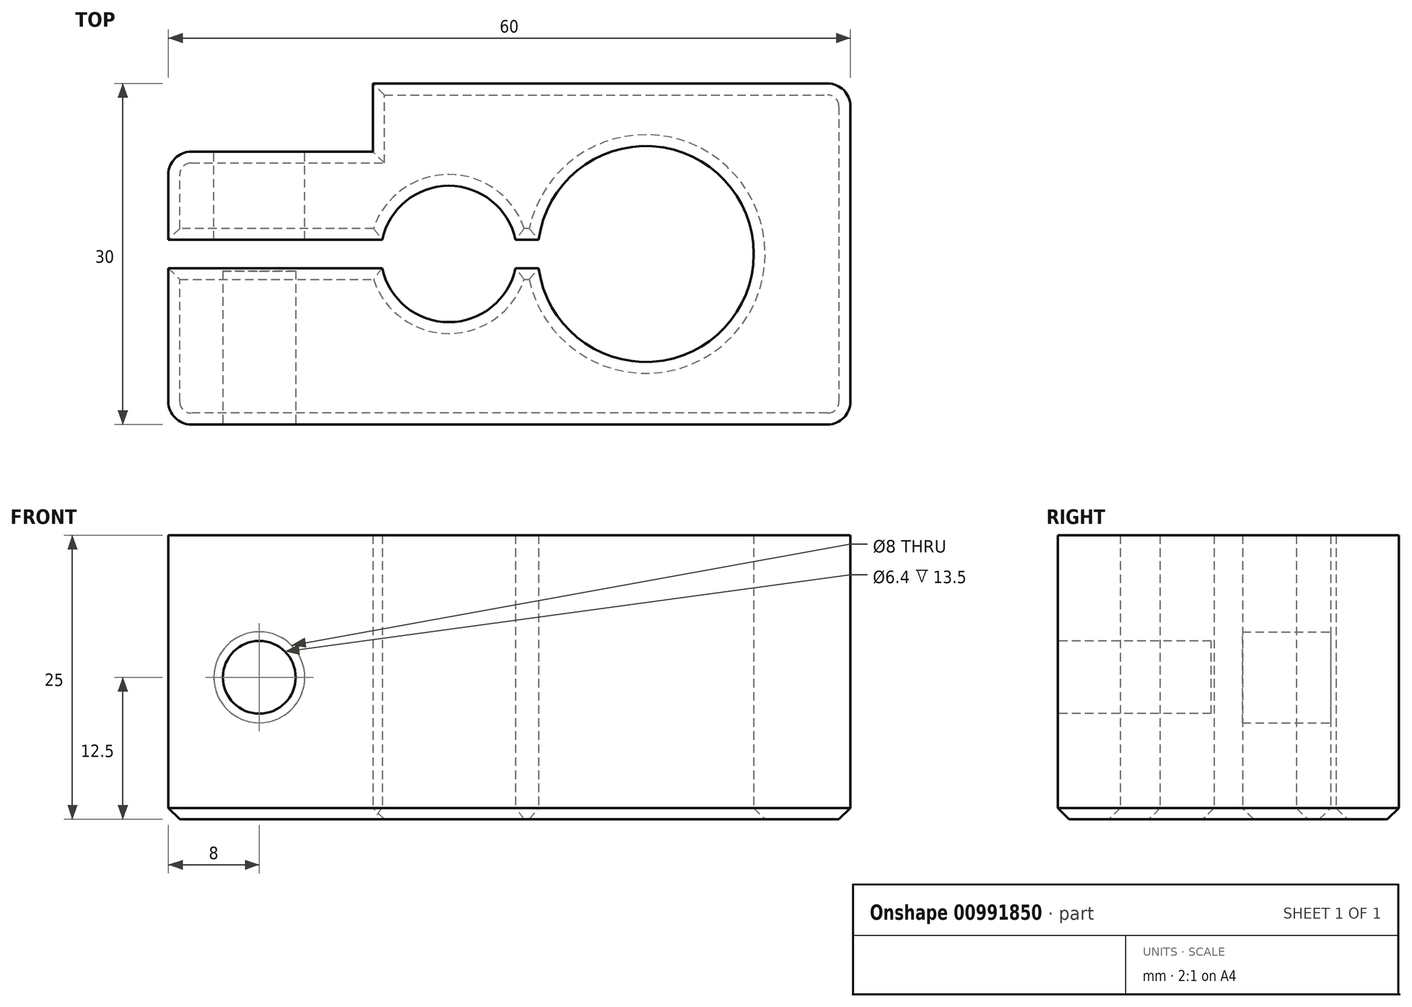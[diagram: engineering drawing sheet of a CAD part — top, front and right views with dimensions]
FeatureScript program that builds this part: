
annotation { "Feature Type Name" : "Feature", "Feature Type Description" : "" }
export const myFeature = defineFeature(function(context is Context, id is Id, definition is map)
    precondition{}
    {
        {
            var Q0;
            Q0=qCreatedBy(makeId("Top.planeOp"),FACE);
            var sketch = newSketch(context, id + "F0", { "sketchPlane" : qUnion([Q0])});
            skLineSegment(sketch, "E0.bottom", {"start": v(-30, -15) * mm, "end": v(30, -15) * mm});
            skLineSegment(sketch, "E0.top", {"start": v(-12, 15) * mm, "end": v(30, 15) * mm});
            skLineSegment(sketch, "E0.left", {"start": v(-30, -15) * mm, "end": v(-30, -1.25) * mm});
            skLineSegment(sketch, "E0.right", {"start": v(30, -15) * mm, "end": v(30, 15) * mm});
            skPoint(sketch, "E0.middle", {"position": v(0, 0) * mm});
            skArc(sketch, "E1", {"start": v(2.58, -1.25) * mm, "mid": v(21.5, 0) * mm, "end": v(2.58, 1.25) * mm});
            skPoint(sketch, "E1.centerSnap0", {"position": v(30, 0) * mm});
            skLineSegment(sketch, "E2.0", {"start": v(2.58, -1.25) * mm, "end": v(0.54, -1.25) * mm});
            skLineSegment(sketch, "E3.MirrorCS", {"start": v(2.58, 1.25) * mm, "end": v(0.54, 1.25) * mm});
            skLineSegment(sketch, "E4.bottom", {"start": v(-30, 9) * mm, "end": v(-12, 9) * mm});
            skLineSegment(sketch, "E4.right", {"start": v(-12, 9) * mm, "end": v(-12, 15) * mm});
            skPoint(sketch, "E5.orphan", {"position": v(-30, 15) * mm});
            skLineSegment(sketch, "E6.trimOffspring", {"start": v(-30, 1.25) * mm, "end": v(-30, 9) * mm});
            skPoint(sketch, "E7.orphan", {"position": v(-30, 0) * mm});
            skPoint(sketch, "E8.orphan", {"position": v(12, 1.25) * mm});
            skPoint(sketch, "E9.orphan", {"position": v(12, -1.25) * mm});
            skArc(sketch, "E10", {"start": v(-11.2, -1.25) * mm, "mid": v(-5.33, -6) * mm, "end": v(0.54, -1.25) * mm});
            skLineSegment(sketch, "E11.trimOffspring", {"start": v(-11.2, 1.25) * mm, "end": v(-30, 1.25) * mm});
            skLineSegment(sketch, "E12.trimOffspring", {"start": v(-11.2, -1.25) * mm, "end": v(-30, -1.25) * mm});
            skArc(sketch, "E13.trimOffspring", {"start": v(0.54, 1.25) * mm, "mid": v(-5.33, 6) * mm, "end": v(-11.2, 1.25) * mm});
            skSolve(sketch);
        }
        {
            var Q0;
            {var subQ0=sQuery(id+"F0.wireOp",EDGE,"vUOmMUN2-ITeZ-OMyY-D1eo-R2V7DhT7ZGRL");var subQ1=sQuery(id+"F0.wireOp",EDGE,"E0.left");var subQ2=makeQuery(id+"F0.imprint","INTERSECT",VERTEX,{"derivedFrom":[subQ1,subQ0]});Q0=makeQuery(id+"F0.imprint","IMPRINT",FACE,{"disambiguationData":[TD([[makeQuery(id+"F0.imprint","IMPRINT",EDGE,{"disambiguationData":[TD([[subQ2,1.0]])],"derivedFrom":subQ1}),-1.0]])]});}
            var Q1;
            {var subQ0=sQuery(id+"F0.wireOp",EDGE,"vUOmMUN2-ITeZ-OMyY-D1eo-R2V7DhT7ZGRL");var subQ1=sQuery(id+"F0.wireOp",EDGE,"E0.left");var subQ2=makeQuery(id+"F0.imprint","INTERSECT",VERTEX,{"derivedFrom":[subQ1,subQ0]});Q1=makeQuery(id+"F0.imprint","IMPRINT",FACE,{"disambiguationData":[TD([[makeQuery(id+"F0.imprint","IMPRINT",EDGE,{"disambiguationData":[TD([[subQ2,-1.0]])],"derivedFrom":subQ1}),-1.0]])]});}
            var Q2;
            {var subQ1=sQuery(id+"F0.wireOp",EDGE,"E0.bottom");Q2=makeQuery(id+"F0.imprint","IMPRINT",FACE,{"disambiguationData":[TD([[makeQuery(id+"F0.imprint","IMPRINT",EDGE,{"derivedFrom":subQ1}),1.0]])]});}
            extrude(context, id + "F1", {"entities" : qUnion([Q0, Q1, Q2]), "depth" : 15 * mm, "offsetDistance" : 25 * mm});
        }
        {
            var Q0;
            Q0 = qSketchRegion(id + "F0", true);
            var Q1;
            Q1=makeQuery(id+"F1.opExtrude","CAP_FACE",FACE,{"disambiguationData":[OSD([sQuery(id+"F0.wireOp",EDGE,"E0.bottom"),sQuery(id+"F0.wireOp",EDGE,"E0.top"),sQuery(id+"F0.wireOp",EDGE,"E0.left"),sQuery(id+"F0.wireOp",EDGE,"E0.right"),sQuery(id+"F0.wireOp",EDGE,"E1"),sQuery(id+"F0.wireOp",EDGE,"E4.bottom"),sQuery(id+"F0.wireOp",EDGE,"E4.right")])],"isStart":true});
            extrude(context, id + "F2", {"entities" : qUnion([Q0, Q1]), "operationType" : NewBodyOperationType.ADD, "depth" : 25 * mm, "offsetDistance" : 25 * mm});
        }
        {
            var Q0;
            Q0 = qSketchRegion(id + "F0", true);
            extrude(context, id + "F3", {"entities" : qUnion([Q0]), "operationType" : NewBodyOperationType.ADD, "depth" : 25 * mm, "offsetDistance" : 25 * mm});
        }
        {
            var Q0;
            {var subQ0=sQuery(id+"F0.wireOp",EDGE,"E4.bottom");Q0=makeQuery(id+"F2.boolean.opBoolean","MERGE",FACE,{"derivedFrom":[makeQuery(id+"F1.opExtrude","SWEPT_FACE",FACE,{"disambiguationData":[OSD([subQ0])]}),makeQuery(id+"F2.opExtrude","SWEPT_FACE",FACE,{"disambiguationData":[OSD([subQ0]),TDD([makeQuery(id+"F0.imprint","IMPRINT",EDGE,{"derivedFrom":subQ0})])]})]});}
            var sketch = newSketch(context, id + "F4", { "sketchPlane" : qUnion([Q0])});
            skCircle(sketch, "E14", {"center": v(22, 12.5) * mm, "radius": 4 * mm});
            skPoint(sketch, "E14.centerSnap0", {"position": v(30, 12.5) * mm});
            skSolve(sketch);
        }
        {
            var Q0;
            Q0=makeQuery(id+"F4.imprint","IMPRINT",FACE,{"disambiguationData":[TD([[makeQuery(id+"F4.imprint","IMPRINT",EDGE,{"derivedFrom":sQuery(id+"F4.wireOp",EDGE,"E14")}),1.0]])]});
            extrude(context, id + "F5", {"entities" : qUnion([Q0]), "operationType" : NewBodyOperationType.REMOVE, "oppositeDirection" : true, "depth" : 9 * mm, "offsetDistance" : 25 * mm});
        }
        {
            var Q0;
            {var subQ0=sQuery(id+"F0.wireOp",EDGE,"E0.bottom");Q0=makeQuery(id+"F2.boolean.opBoolean","MERGE",FACE,{"derivedFrom":[makeQuery(id+"F1.opExtrude","SWEPT_FACE",FACE,{"disambiguationData":[OSD([subQ0])]}),makeQuery(id+"F2.opExtrude","SWEPT_FACE",FACE,{"disambiguationData":[OSD([subQ0]),TDD([makeQuery(id+"F0.imprint","IMPRINT",EDGE,{"derivedFrom":subQ0})])]})]});}
            var sketch = newSketch(context, id + "F6", { "sketchPlane" : qUnion([Q0])});
            skCircle(sketch, "E15", {"center": v(-22, 12.5) * mm, "radius": 3.2 * mm});
            skPoint(sketch, "E15.centerSnap0", {"position": v(-30, 12.5) * mm});
            skSolve(sketch);
        }
        {
            var Q0;
            Q0 = qSketchRegion(id + "F6", true);
            extrude(context, id + "F7", {"entities" : qUnion([Q0]), "operationType" : NewBodyOperationType.REMOVE, "oppositeDirection" : true, "depth" : 13.5 * mm, "offsetDistance" : 25 * mm});
        }
        {
            var Q0;
            {var subQ0=sQuery(id+"F0.wireOp",EDGE,"E0.right");var subQ1=sQuery(id+"F0.wireOp",EDGE,"E0.bottom");Q0=makeQuery(id+"F2.boolean.opBoolean","MERGE",EDGE,{"derivedFrom":[makeQuery(id+"F1.opExtrude","SWEPT_EDGE",EDGE,{"disambiguationData":[OSD([subQ1,subQ0])]}),makeQuery(id+"F2.opExtrude","SWEPT_EDGE",EDGE,{"disambiguationData":[OSD([subQ1,subQ0]),TDD([makeQuery(id+"F0.imprint","INTERSECT",VERTEX,{"derivedFrom":[subQ1,subQ0]})])]})]});}
            var Q1;
            {var subQ0=sQuery(id+"F0.wireOp",EDGE,"E0.right");var subQ1=sQuery(id+"F0.wireOp",EDGE,"E0.top");Q1=makeQuery(id+"F2.boolean.opBoolean","MERGE",EDGE,{"derivedFrom":[makeQuery(id+"F1.opExtrude","SWEPT_EDGE",EDGE,{"disambiguationData":[OSD([subQ1,subQ0])]}),makeQuery(id+"F2.opExtrude","SWEPT_EDGE",EDGE,{"disambiguationData":[OSD([subQ1,subQ0]),TDD([makeQuery(id+"F0.imprint","INTERSECT",VERTEX,{"derivedFrom":[subQ1,subQ0]})])]})]});}
            var Q2;
            {var subQ0=sQuery(id+"F0.wireOp",EDGE,"E0.left");var subQ1=sQuery(id+"F0.wireOp",EDGE,"E0.bottom");Q2=makeQuery(id+"F2.boolean.opBoolean","MERGE",EDGE,{"derivedFrom":[makeQuery(id+"F1.opExtrude","SWEPT_EDGE",EDGE,{"disambiguationData":[OSD([subQ1,subQ0])]}),makeQuery(id+"F2.opExtrude","SWEPT_EDGE",EDGE,{"disambiguationData":[OSD([subQ1,subQ0]),TDD([makeQuery(id+"F0.imprint","INTERSECT",VERTEX,{"derivedFrom":[subQ1,subQ0]})])]})]});}
            var Q3;
            {var subQ0=sQuery(id+"F0.wireOp",EDGE,"E6.trimOffspring");var subQ1=sQuery(id+"F0.wireOp",EDGE,"E4.bottom");Q3=makeQuery(id+"F2.boolean.opBoolean","MERGE",EDGE,{"derivedFrom":[makeQuery(id+"F1.opExtrude","SWEPT_EDGE",EDGE,{"disambiguationData":[OSD([subQ1,subQ0])]}),makeQuery(id+"F2.opExtrude","SWEPT_EDGE",EDGE,{"disambiguationData":[OSD([subQ1,subQ0]),TDD([makeQuery(id+"F0.imprint","INTERSECT",VERTEX,{"derivedFrom":[subQ1,subQ0]})])]})]});}
            fillet(context, id + "F8", {"entities" : qUnion([Q0, Q1, Q2, Q3]), "radius" : 2 * mm, "tangentPropagation" : true, "allowEdgeOverflow" : false});
        }
        {
            var Q0;
            Q0=makeQuery(id+"F1.opExtrude","CAP_FACE",FACE,{"disambiguationData":[OSD([sQuery(id+"F0.wireOp",EDGE,"E0.bottom"),sQuery(id+"F0.wireOp",EDGE,"E0.top"),sQuery(id+"F0.wireOp",EDGE,"E0.left"),sQuery(id+"F0.wireOp",EDGE,"E0.right"),sQuery(id+"F0.wireOp",EDGE,"E1"),sQuery(id+"F0.wireOp",EDGE,"E2.0"),sQuery(id+"F0.wireOp",EDGE,"E3.MirrorCS"),sQuery(id+"F0.wireOp",EDGE,"E4.bottom"),sQuery(id+"F0.wireOp",EDGE,"E4.right"),sQuery(id+"F0.wireOp",EDGE,"E6.trimOffspring"),sQuery(id+"F0.wireOp",EDGE,"E10"),sQuery(id+"F0.wireOp",EDGE,"E11.trimOffspring"),sQuery(id+"F0.wireOp",EDGE,"E12.trimOffspring"),sQuery(id+"F0.wireOp",EDGE,"E13.trimOffspring")])],"isStart":true});
            chamfer(context, id + "F9", {"entities" : qUnion([Q0]), "width" : 1 * mm, "tangentPropagation" : true});
        }
    });
